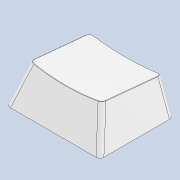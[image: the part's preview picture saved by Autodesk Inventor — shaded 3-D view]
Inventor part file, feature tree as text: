
AUTODESK INVENTOR PART (.ipt)
format: ipt  version: 2021 (Build 250183000, 183)  size: 249,344 bytes
history: native  units: in
note: dims shown in document units (in); Inventor stores cm internally (conversion verified against a paired STEP export)
features: chamfer x1
ambient origin geometry x8: Origin, YZ Plane, XZ Plane, XY Plane, X Axis, Y Axis, Z Axis, Center Point
bodies: Solid1 (feature_tree)
feature tree (1):
  chamfer  "Chamfer1"  [1 undecoded]
note: 1 required parameter value undecoded (feature->parameter linkage not recoverable at this tier; creation-order binding heuristic only, values carry confidence <= 0.55)
